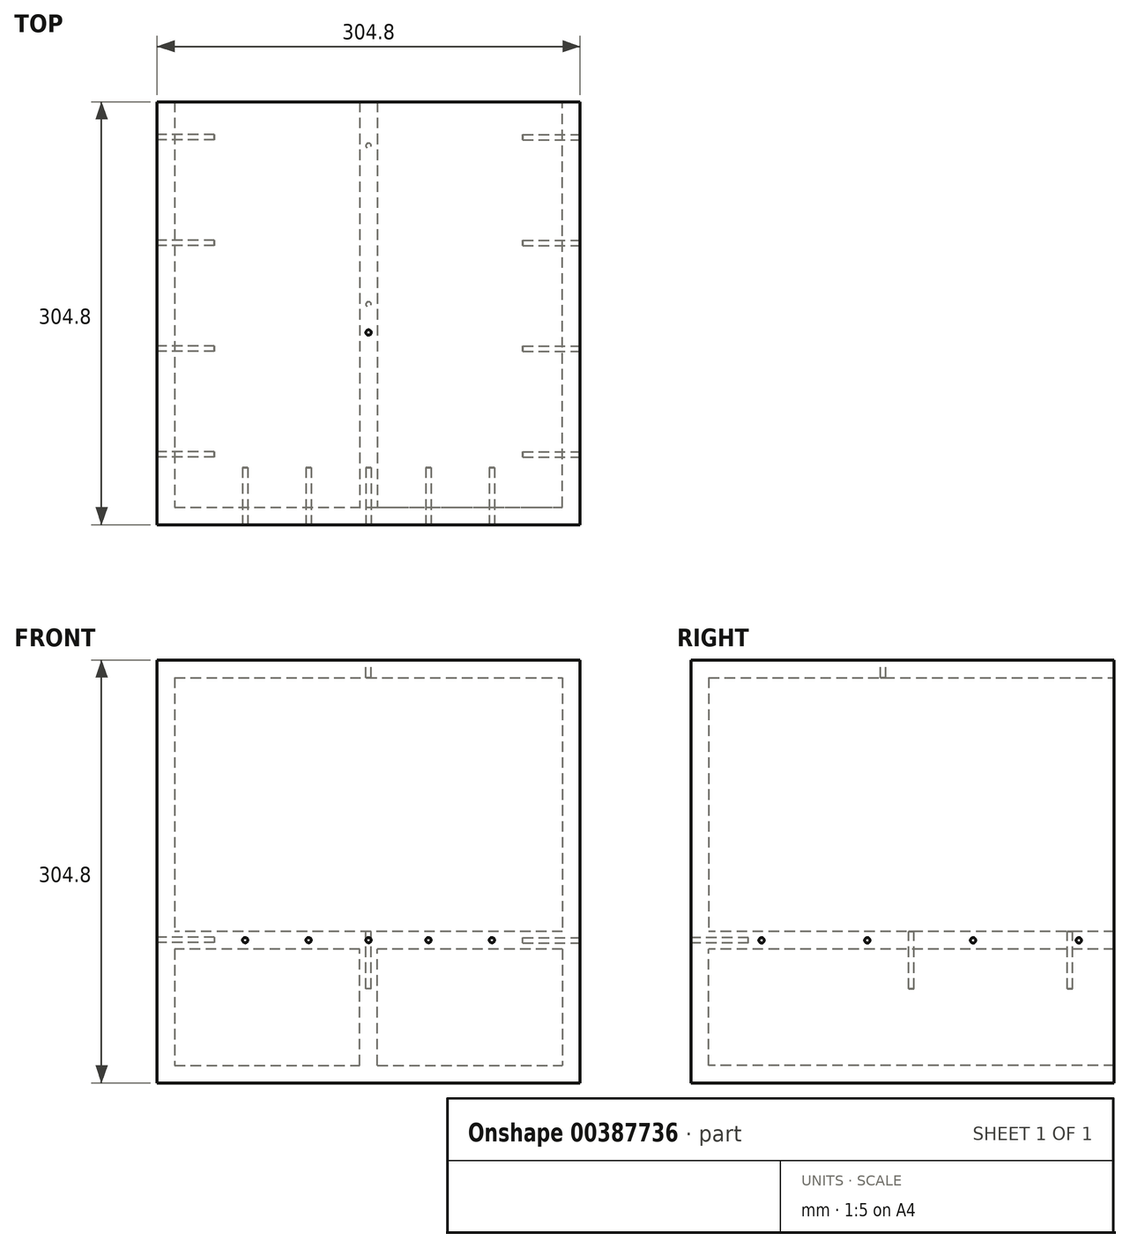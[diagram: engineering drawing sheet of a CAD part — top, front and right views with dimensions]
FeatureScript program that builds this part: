
annotation { "Feature Type Name" : "Feature", "Feature Type Description" : "" }
export const myFeature = defineFeature(function(context is Context, id is Id, definition is map)
    precondition{}
    {
        {
            var Q0;
            Q0=qCreatedBy(makeId("Front.planeOp"),FACE);
            var sketch = newSketch(context, id + "F0", { "sketchPlane" : qUnion([Q0])});
            skLineSegment(sketch, "E0.bottom", {"start": v(-152.64, 192.2) * mm, "end": v(152.16, 192.2) * mm});
            skLineSegment(sketch, "E0.top", {"start": v(-152.64, -112.6) * mm, "end": v(152.16, -112.6) * mm});
            skLineSegment(sketch, "E0.left", {"start": v(-152.64, 192.2) * mm, "end": v(-152.64, -112.6) * mm});
            skLineSegment(sketch, "E0.right", {"start": v(152.16, 192.2) * mm, "end": v(152.16, -112.6) * mm});
            skSolve(sketch);
        }
        {
            var Q0;
            Q0 = qSketchRegion(id + "F0", true);
            extrude(context, id + "F1", {"entities" : qUnion([Q0]), "depth" : 304.8 * mm});
        }
        {
            var Q0;
            Q0=makeQuery(id+"F1.opExtrude","CAP_FACE",FACE,{"disambiguationData":[OSD([sQuery(id+"F0.wireOp",EDGE,"E0.bottom"),sQuery(id+"F0.wireOp",EDGE,"E0.top"),sQuery(id+"F0.wireOp",EDGE,"E0.left"),sQuery(id+"F0.wireOp",EDGE,"E0.right")])],"isStart":true});
            shell(context, id + "F2", {"entities" : qUnion([Q0]), "thickness" : 12.7 * mm});
        }
        {
            var Q0;
            Q0=makeQuery(id+"F2.opShell","OFFSET_FACE",FACE,{"disambiguationData":[OSD([sQuery(id+"F0.wireOp",EDGE,"E0.bottom"),sQuery(id+"F0.wireOp",EDGE,"E0.top"),sQuery(id+"F0.wireOp",EDGE,"E0.left"),sQuery(id+"F0.wireOp",EDGE,"E0.right")])]});
            var sketch = newSketch(context, id + "F3", { "sketchPlane" : qUnion([Q0])});
            skLineSegment(sketch, "E1.bottom", {"start": v(-139.46, -3.52) * mm, "end": v(139.94, -3.52) * mm});
            skLineSegment(sketch, "E1.top", {"start": v(-139.46, -16.22) * mm, "end": v(139.94, -16.22) * mm});
            skLineSegment(sketch, "E1.left", {"start": v(-139.46, -3.52) * mm, "end": v(-139.46, -16.22) * mm});
            skLineSegment(sketch, "E1.right", {"start": v(139.94, -3.52) * mm, "end": v(139.94, -16.22) * mm});
            skSolve(sketch);
        }
        {
            var Q0;
            Q0 = qSketchRegion(id + "F3", true);
            extrude(context, id + "F4", {"entities" : qUnion([Q0]), "operationType" : NewBodyOperationType.ADD, "depth" : 292.1 * mm});
        }
        {
            var Q0;
            Q0=makeQuery(id+"F1.opExtrude","SWEPT_FACE",FACE,{"disambiguationData":[OSD([sQuery(id+"F0.wireOp",EDGE,"E0.bottom")])]});
            var sketch = newSketch(context, id + "F5", { "sketchPlane" : qUnion([Q0])});
            skCircle(sketch, "E2", {"center": v(-0.24, -166.32) * mm, "radius": 1.9 * mm});
            skSolve(sketch);
        }
        {
            var Q0;
            Q0 = qSketchRegion(id + "F5", true);
            extrude(context, id + "F6", {"entities" : qUnion([Q0]), "operationType" : NewBodyOperationType.REMOVE, "endBound" : BoundingType.SYMMETRIC, "oppositeDirection" : true, "depth" : 25.4 * mm});
        }
        {
            var Q0;
            Q0=makeQuery(id+"F1.opExtrude","SWEPT_FACE",FACE,{"disambiguationData":[OSD([sQuery(id+"F0.wireOp",EDGE,"E0.right")])]});
            var sketch = newSketch(context, id + "F7", { "sketchPlane" : qUnion([Q0])});
            skCircle(sketch, "E3", {"center": v(-254, -9.87) * mm, "radius": 1.9 * mm});
            skCircle(sketch, "E4", {"center": v(-177.8, -9.87) * mm, "radius": 1.9 * mm});
            skCircle(sketch, "E5", {"center": v(-101.6, -9.87) * mm, "radius": 1.9 * mm});
            skCircle(sketch, "E6", {"center": v(-25.4, -9.87) * mm, "radius": 1.9 * mm});
            skSolve(sketch);
        }
        {
            var Q0;
            Q0 = qSketchRegion(id + "F7", true);
            extrude(context, id + "F8", {"entities" : qUnion([Q0]), "operationType" : NewBodyOperationType.REMOVE, "oppositeDirection" : true, "depth" : 41.27 * mm});
        }
        {
            var Q0;
            Q0=makeQuery(id+"F1.opExtrude","SWEPT_FACE",FACE,{"disambiguationData":[OSD([sQuery(id+"F0.wireOp",EDGE,"E0.left")])]});
            var sketch = newSketch(context, id + "F9", { "sketchPlane" : qUnion([Q0])});
            skCircle(sketch, "E7", {"center": v(25.4, -9.67) * mm, "radius": 1.9 * mm});
            skCircle(sketch, "E8", {"center": v(101.6, -9.67) * mm, "radius": 1.9 * mm});
            skCircle(sketch, "E9", {"center": v(177.8, -9.67) * mm, "radius": 1.9 * mm});
            skCircle(sketch, "E10", {"center": v(254, -9.66) * mm, "radius": 1.9 * mm});
            skSolve(sketch);
        }
        {
            var Q0;
            Q0 = qSketchRegion(id + "F9", true);
            extrude(context, id + "F10", {"entities" : qUnion([Q0]), "operationType" : NewBodyOperationType.REMOVE, "oppositeDirection" : true, "depth" : 41.27 * mm});
        }
        {
            var Q0;
            Q0=makeQuery(id+"F1.opExtrude","CAP_FACE",FACE,{"disambiguationData":[OSD([sQuery(id+"F0.wireOp",EDGE,"E0.bottom"),sQuery(id+"F0.wireOp",EDGE,"E0.top"),sQuery(id+"F0.wireOp",EDGE,"E0.left"),sQuery(id+"F0.wireOp",EDGE,"E0.right")])],"isStart":false});
            var sketch = newSketch(context, id + "F11", { "sketchPlane" : qUnion([Q0])});
            skCircle(sketch, "E11", {"center": v(-89.14, -9.73) * mm, "radius": 1.9 * mm});
            skCircle(sketch, "E12", {"center": v(-43.42, -9.73) * mm, "radius": 1.9 * mm});
            skCircle(sketch, "E13", {"center": v(-0.24, -9.73) * mm, "radius": 1.9 * mm});
            skCircle(sketch, "E14", {"center": v(42.94, -9.73) * mm, "radius": 1.9 * mm});
            skCircle(sketch, "E15", {"center": v(88.66, -9.73) * mm, "radius": 1.9 * mm});
            skSolve(sketch);
        }
        {
            var Q0;
            Q0 = qSketchRegion(id + "F11", true);
            extrude(context, id + "F12", {"entities" : qUnion([Q0]), "operationType" : NewBodyOperationType.REMOVE, "oppositeDirection" : true, "depth" : 41.27 * mm});
        }
        {
            var Q0;
            {var subQ0=sQuery(id+"F0.wireOp",EDGE,"E0.top");var subQ1=sQuery(id+"F0.wireOp",EDGE,"E0.left");var subQ2=sQuery(id+"F0.wireOp",EDGE,"E0.right");Q0=makeQuery(id+"F4.boolean.opBoolean","SPLIT",FACE,{"disambiguationData":[TD([makeQuery(id+"F2.opShell","OFFSET_FACE",FACE,{"disambiguationData":[OSD([subQ0])]})])],"derivedFrom":makeQuery(id+"F2.opShell","OFFSET_FACE",FACE,{"disambiguationData":[OSD([sQuery(id+"F0.wireOp",EDGE,"E0.bottom"),subQ0,subQ1,subQ2])]})});}
            var sketch = newSketch(context, id + "F13", { "sketchPlane" : qUnion([Q0])});
            skLineSegment(sketch, "E16.bottom", {"start": v(-6.1, -99.9) * mm, "end": v(6.6, -99.9) * mm});
            skLineSegment(sketch, "E16.top", {"start": v(-6.1, -16.22) * mm, "end": v(6.6, -16.22) * mm});
            skLineSegment(sketch, "E16.left", {"start": v(-6.1, -99.9) * mm, "end": v(-6.1, -16.22) * mm});
            skLineSegment(sketch, "E16.right", {"start": v(6.6, -99.9) * mm, "end": v(6.6, -16.22) * mm});
            skSolve(sketch);
        }
        {
            var Q0;
            Q0 = qSketchRegion(id + "F13", true);
            extrude(context, id + "F14", {"entities" : qUnion([Q0]), "operationType" : NewBodyOperationType.ADD, "depth" : 292.1 * mm});
        }
        {
            var Q0;
            Q0=makeQuery(id+"F4.opExtrude","SWEPT_FACE",FACE,{"disambiguationData":[OSD([sQuery(id+"F3.wireOp",EDGE,"E1.bottom")])]});
            var sketch = newSketch(context, id + "F15", { "sketchPlane" : qUnion([Q0])});
            skCircle(sketch, "E17", {"center": v(-0.24, -31.75) * mm, "radius": 1.9 * mm});
            skCircle(sketch, "E18", {"center": v(-0.24, -146.05) * mm, "radius": 1.9 * mm});
            skSolve(sketch);
        }
        {
            var Q0;
            Q0 = qSketchRegion(id + "F15", true);
            extrude(context, id + "F16", {"entities" : qUnion([Q0]), "operationType" : NewBodyOperationType.REMOVE, "oppositeDirection" : true, "depth" : 41.27 * mm});
        }
    });
